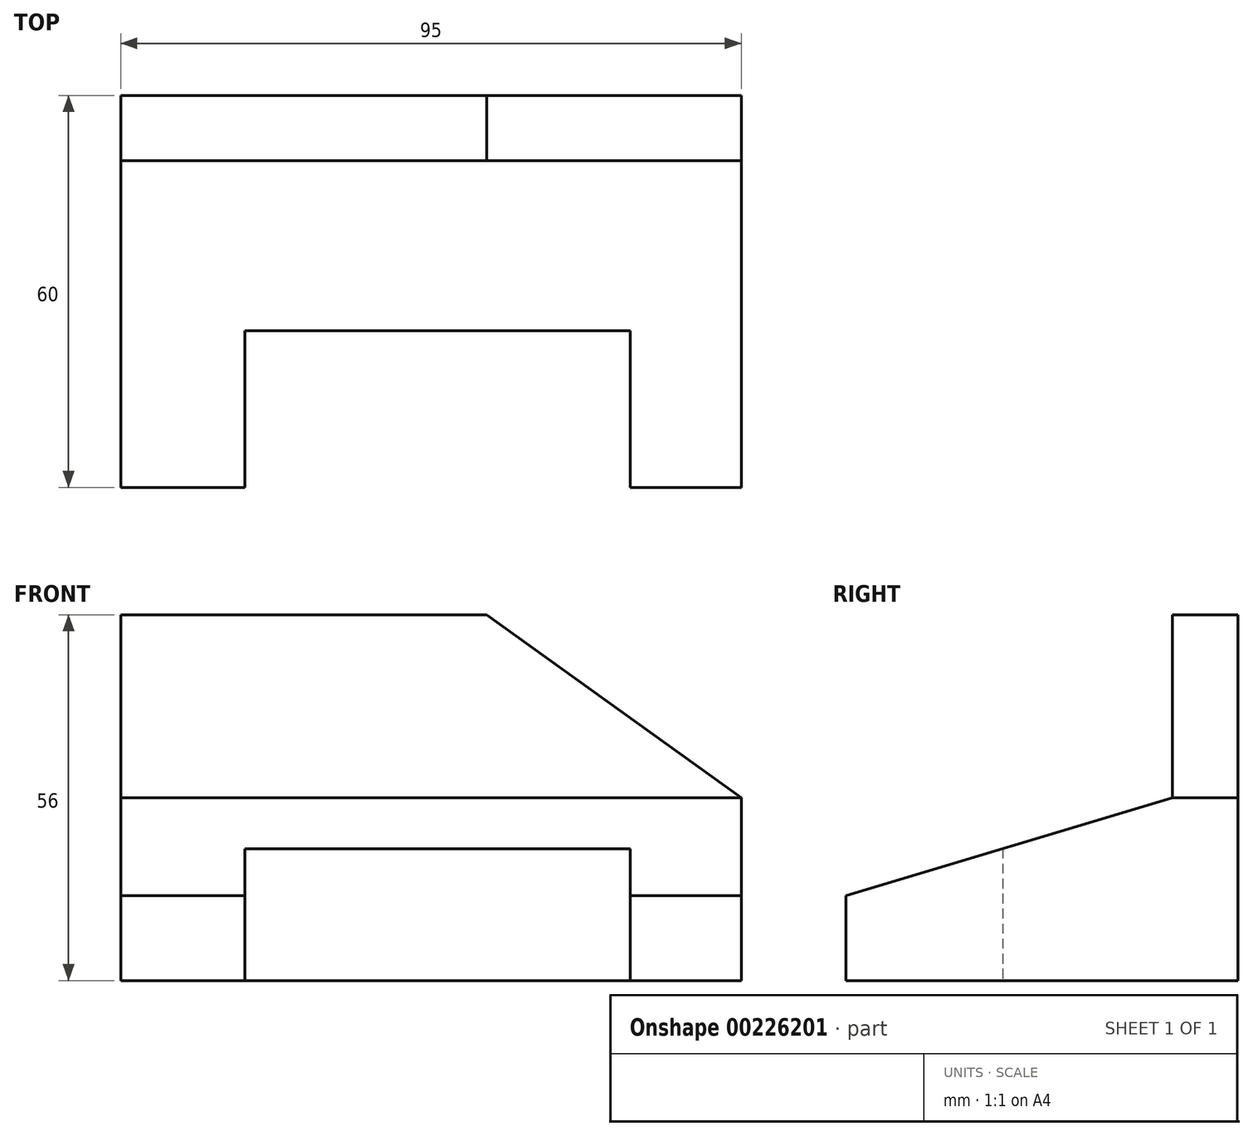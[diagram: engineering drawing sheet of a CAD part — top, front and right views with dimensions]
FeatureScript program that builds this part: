
annotation { "Feature Type Name" : "Feature", "Feature Type Description" : "" }
export const myFeature = defineFeature(function(context is Context, id is Id, definition is map)
    precondition{}
    {
        {
            var Q0;
            Q0=qCreatedBy(makeId("Right.planeOp"),FACE);
            var sketch = newSketch(context, id + "F0", { "sketchPlane" : qUnion([Q0])});
            skLineSegment(sketch, "E0", {"start": v(0, 0) * mm, "end": v(0, 56) * mm});
            skLineSegment(sketch, "E1", {"start": v(0, 56) * mm, "end": v(-10, 56) * mm});
            skLineSegment(sketch, "E2", {"start": v(-10, 56) * mm, "end": v(-10, 28) * mm});
            skLineSegment(sketch, "E3", {"start": v(-10, 28) * mm, "end": v(-60, 13) * mm});
            skLineSegment(sketch, "E4", {"start": v(-60, 13) * mm, "end": v(-60, 0) * mm});
            skLineSegment(sketch, "E5", {"start": v(-60, 0) * mm, "end": v(0, 0) * mm});
            skSolve(sketch);
        }
        {
            var Q0;
            Q0 = qSketchRegion(id + "F0", true);
            extrude(context, id + "F1", {"entities" : qUnion([Q0]), "oppositeDirection" : true, "depth" : 95 * mm});
        }
        {
            var Q0;
            Q0=makeQuery(id+"F1.opExtrude","SWEPT_FACE",FACE,{"disambiguationData":[OSD([sQuery(id+"F0.wireOp",EDGE,"E2")])]});
            var sketch = newSketch(context, id + "F2", { "sketchPlane" : qUnion([Q0])});
            skLineSegment(sketch, "E6", {"start": v(0, 28) * mm, "end": v(-39, 56) * mm});
            skSolve(sketch);
        }
        {
            var Q0;
            {var subQ0=sQuery(id+"F2.wireOp",EDGE,"E6");Q0=makeQuery(id+"F2.imprint","IMPRINT",FACE,{"disambiguationData":[TD([[makeQuery(id+"F2.imprint","IMPRINT",EDGE,{"derivedFrom":subQ0}),-1.0]])]});}
            extrude(context, id + "F3", {"entities" : qUnion([Q0]), "operationType" : NewBodyOperationType.REMOVE, "oppositeDirection" : true, "depth" : 45.5 * mm});
        }
        {
            var Q0;
            Q0=makeQuery(id+"F1.opExtrude","SWEPT_FACE",FACE,{"disambiguationData":[OSD([sQuery(id+"F0.wireOp",EDGE,"E5")])]});
            var sketch = newSketch(context, id + "F4", { "sketchPlane" : qUnion([Q0])});
            skLineSegment(sketch, "E7.bottom", {"start": v(-76, 60) * mm, "end": v(-17, 60) * mm});
            skLineSegment(sketch, "E7.top", {"start": v(-76, 36) * mm, "end": v(-17, 36) * mm});
            skLineSegment(sketch, "E7.left", {"start": v(-76, 60) * mm, "end": v(-76, 36) * mm});
            skLineSegment(sketch, "E7.right", {"start": v(-17, 60) * mm, "end": v(-17, 36) * mm});
            skSolve(sketch);
        }
        {
            var Q0;
            Q0 = qSketchRegion(id + "F4", true);
            extrude(context, id + "F5", {"entities" : qUnion([Q0]), "operationType" : NewBodyOperationType.REMOVE, "oppositeDirection" : true, "depth" : 95 * mm});
        }
    });
